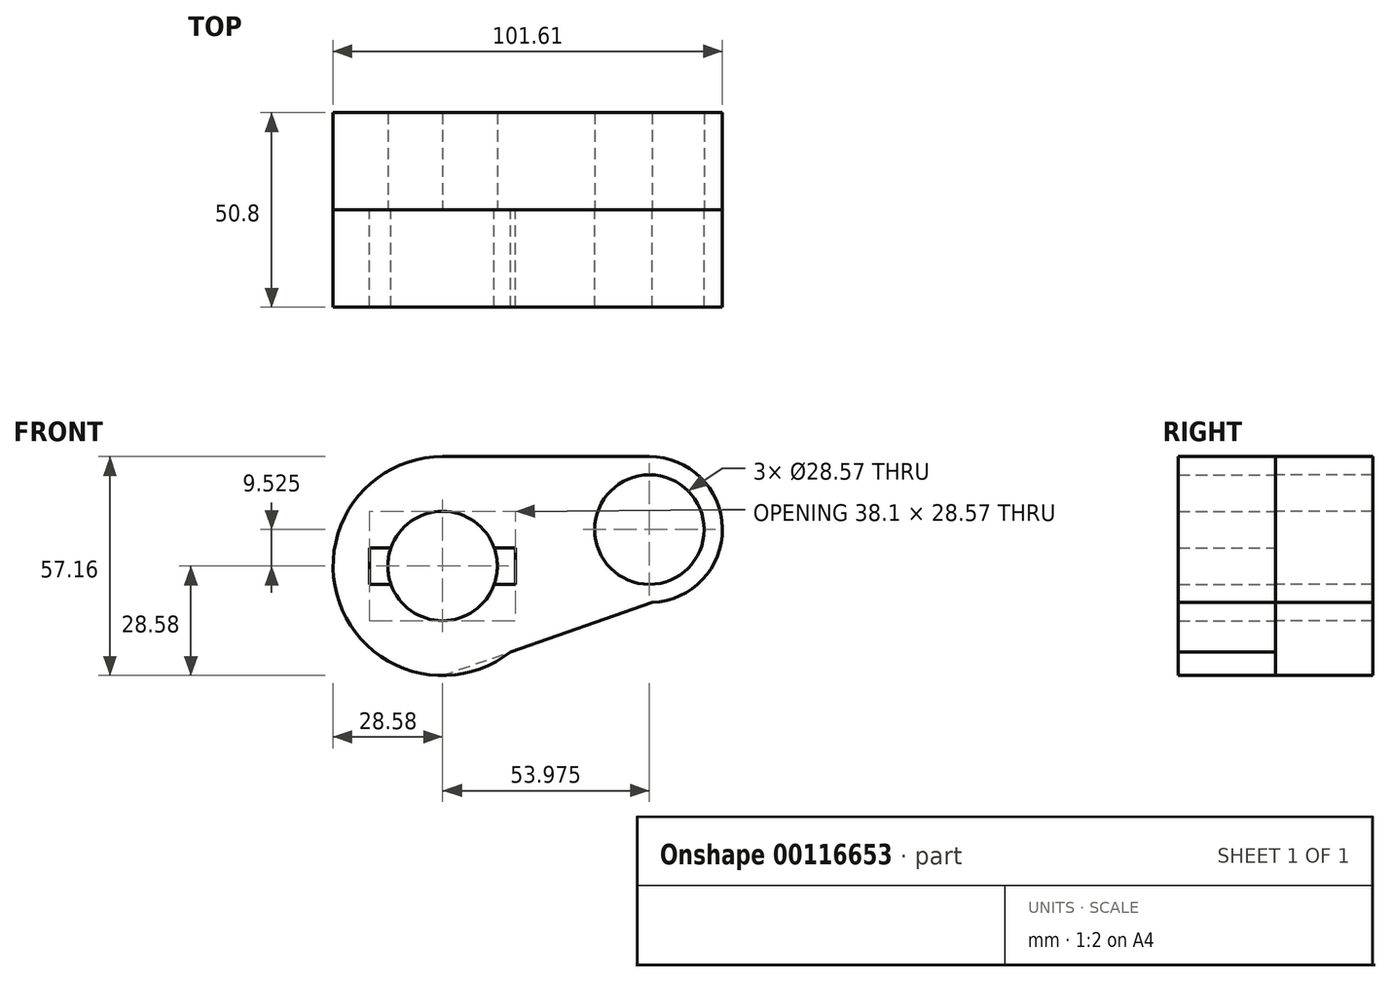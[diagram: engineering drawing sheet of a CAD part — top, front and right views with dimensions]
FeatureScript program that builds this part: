
annotation { "Feature Type Name" : "Feature", "Feature Type Description" : "" }
export const myFeature = defineFeature(function(context is Context, id is Id, definition is map)
    precondition{}
    {
        {
            var Q0;
            Q0=qCreatedBy(makeId("Front.planeOp"),FACE);
            var sketch = newSketch(context, id + "F0", { "sketchPlane" : qUnion([Q0])});
            skCircle(sketch, "E0", {"center": v(0, 0) * mm, "radius": 28.58 * mm});
            skCircle(sketch, "E1", {"center": v(53.97, 9.53) * mm, "radius": 19.05 * mm});
            skLineSegment(sketch, "E2", {"start": v(0, 28.58) * mm, "end": v(53.97, 28.58) * mm});
            skCircle(sketch, "E3", {"center": v(0, 0) * mm, "radius": 14.29 * mm});
            skCircle(sketch, "E4", {"center": v(53.97, 9.53) * mm, "radius": 14.29 * mm});
            skLineSegment(sketch, "E5.bottom", {"start": v(-19.05, -4.76) * mm, "end": v(19.05, -4.76) * mm});
            skLineSegment(sketch, "E5.top", {"start": v(-19.05, 4.76) * mm, "end": v(19.05, 4.76) * mm});
            skLineSegment(sketch, "E5.left", {"start": v(-19.05, -4.76) * mm, "end": v(-19.05, 4.76) * mm});
            skLineSegment(sketch, "E5.right", {"start": v(19.05, -4.76) * mm, "end": v(19.05, 4.76) * mm});
            skLineSegment(sketch, "E6", {"start": v(0, -28.57) * mm, "end": v(54.71, -9.51) * mm});
            skSolve(sketch);
        }
        {
            var Q0;
            {var subQ0=sQuery(id+"F0.wireOp",EDGE,"E2");Q0=makeQuery(id+"F0.imprint","IMPRINT",FACE,{"disambiguationData":[TD([[makeQuery(id+"F0.imprint","IMPRINT",EDGE,{"derivedFrom":subQ0}),-1.0]])]});}
            var Q1;
            {var subQ4=sQuery(id+"F0.wireOp",EDGE,"E5.left");Q1=makeQuery(id+"F0.imprint","IMPRINT",FACE,{"disambiguationData":[TD([[makeQuery(id+"F0.imprint","IMPRINT",EDGE,{"derivedFrom":subQ4}),1.0]])]});}
            var Q2;
            Q2=makeQuery(id+"F0.imprint","IMPRINT",FACE,{"disambiguationData":[TD([[makeQuery(id+"F0.imprint","IMPRINT",EDGE,{"derivedFrom":sQuery(id+"F0.wireOp",EDGE,"E4")}),-1.0]])]});
            var Q3;
            {var subQ5=sQuery(id+"F0.wireOp",EDGE,"E5.right");Q3=makeQuery(id+"F0.imprint","IMPRINT",FACE,{"disambiguationData":[TD([[makeQuery(id+"F0.imprint","IMPRINT",EDGE,{"derivedFrom":subQ5}),1.0]])]});}
            var Q4;
            {var subQ5=sQuery(id+"F0.wireOp",EDGE,"E5.right");Q4=makeQuery(id+"F0.imprint","IMPRINT",FACE,{"disambiguationData":[TD([[makeQuery(id+"F0.imprint","IMPRINT",EDGE,{"derivedFrom":subQ5}),1.0]])]});}
            var Q5;
            {var subQ5=sQuery(id+"F0.wireOp",EDGE,"E5.left");Q5=makeQuery(id+"F0.imprint","IMPRINT",FACE,{"disambiguationData":[TD([[makeQuery(id+"F0.imprint","IMPRINT",EDGE,{"derivedFrom":subQ5}),-1.0]])]});}
            var Q6;
            {var subQ0=sQuery(id+"F0.wireOp",EDGE,"E6");var subQ1=sQuery(id+"F0.wireOp",EDGE,"E0");var subQ2=makeQuery(id+"F0.imprint","INTERSECT",VERTEX,{"disambiguationData":[OD(0.0)],"derivedFrom":[subQ1,subQ0]});Q6=makeQuery(id+"F0.imprint","IMPRINT",FACE,{"disambiguationData":[TD([[makeQuery(id+"F0.imprint","IMPRINT",EDGE,{"disambiguationData":[TD([[subQ2,-1.0]])],"derivedFrom":subQ1}),1.0]])]});}
            extrude(context, id + "F1", {"entities" : qUnion([Q0, Q1, Q2, Q3, Q4, Q5, Q6]), "oppositeDirection" : true, "depth" : 25.4 * mm});
        }
        {
            var Q0;
            Q0 = qSketchRegion(id + "F0", true);
            extrude(context, id + "F2", {"entities" : qUnion([Q0]), "depth" : 25.4 * mm});
        }
    });
